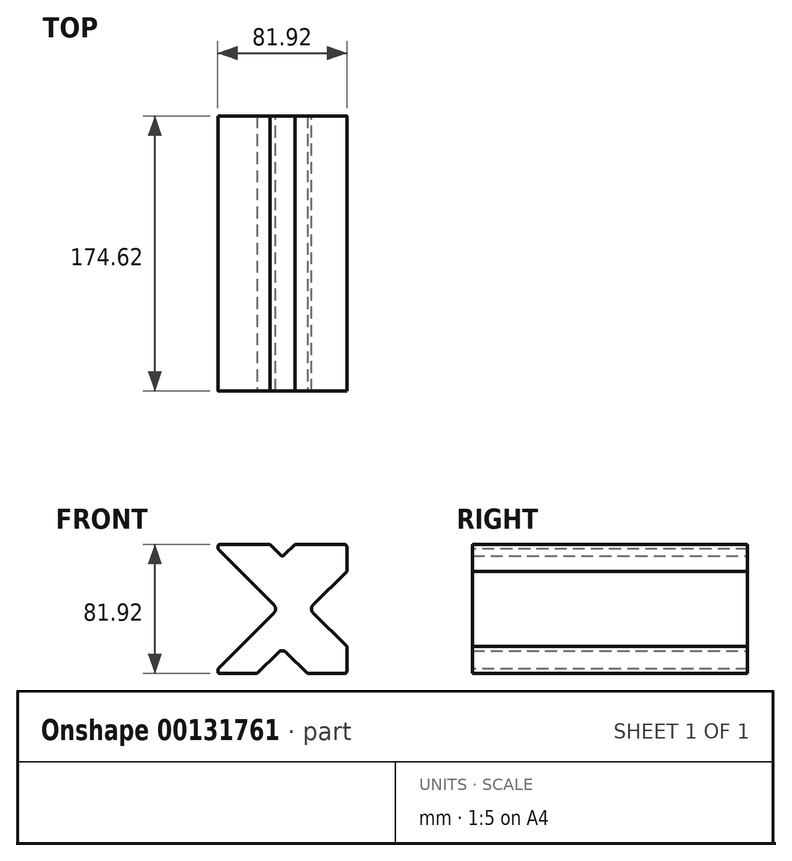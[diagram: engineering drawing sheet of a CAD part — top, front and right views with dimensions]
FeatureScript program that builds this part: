
annotation { "Feature Type Name" : "Feature", "Feature Type Description" : "" }
export const myFeature = defineFeature(function(context is Context, id is Id, definition is map)
    precondition{}
    {
        {
            var Q0;
            Q0=qCreatedBy(makeId("Front.planeOp"),FACE);
            var sketch = newSketch(context, id + "F0", { "sketchPlane" : qUnion([Q0])});
            skLineSegment(sketch, "E0.bottom", {"start": v(40.96, -40.96) * mm, "end": v(-40.96, -40.96) * mm});
            skLineSegment(sketch, "E0.top", {"start": v(40.96, 40.96) * mm, "end": v(-40.96, 40.96) * mm});
            skLineSegment(sketch, "E0.left", {"start": v(40.96, -40.96) * mm, "end": v(40.96, 40.96) * mm});
            skLineSegment(sketch, "E0.right", {"start": v(-40.96, -40.96) * mm, "end": v(-40.96, 40.96) * mm});
            skPoint(sketch, "E0.middle", {"position": v(0, 0) * mm});
            skSolve(sketch);
        }
        {
            var Q0;
            Q0 = qSketchRegion(id + "F0", true);
            extrude(context, id + "F1", {"entities" : qUnion([Q0]), "depth" : 174.62 * mm, "offsetDistance" : 25.4 * mm});
        }
        {
            var Q0;
            Q0=makeQuery(id+"F1.opExtrude","CAP_FACE",FACE,{"disambiguationData":[OSD([sQuery(id+"F0.wireOp",EDGE,"E0.bottom"),sQuery(id+"F0.wireOp",EDGE,"E0.top"),sQuery(id+"F0.wireOp",EDGE,"E0.left"),sQuery(id+"F0.wireOp",EDGE,"E0.right")])],"isStart":false});
            var sketch = newSketch(context, id + "F2", { "sketchPlane" : qUnion([Q0])});
            skLineSegment(sketch, "E1", {"start": v(-7.94, 40.96) * mm, "end": v(0, 33.02) * mm});
            skLineSegment(sketch, "E2", {"start": v(0, 33.02) * mm, "end": v(7.94, 40.96) * mm});
            skLineSegment(sketch, "E3", {"start": v(7.94, 40.96) * mm, "end": v(-7.94, 40.96) * mm});
            skSolve(sketch);
        }
        {
            var Q0;
            Q0 = qSketchRegion(id + "F2", true);
            extrude(context, id + "F3", {"entities" : qUnion([Q0]), "operationType" : NewBodyOperationType.REMOVE, "endBound" : BoundingType.THROUGH_ALL, "oppositeDirection" : true, "depth" : 25.4 * mm, "offsetDistance" : 25.4 * mm});
        }
        {
            var Q0;
            Q0=makeQuery(id+"F1.opExtrude","CAP_FACE",FACE,{"disambiguationData":[OSD([sQuery(id+"F0.wireOp",EDGE,"E0.bottom"),sQuery(id+"F0.wireOp",EDGE,"E0.top"),sQuery(id+"F0.wireOp",EDGE,"E0.left"),sQuery(id+"F0.wireOp",EDGE,"E0.right")])],"isStart":false});
            var sketch = newSketch(context, id + "F4", { "sketchPlane" : qUnion([Q0])});
            skLineSegment(sketch, "E4", {"start": v(-15.87, -40.96) * mm, "end": v(0, -25.08) * mm});
            skLineSegment(sketch, "E5", {"start": v(0, -25.08) * mm, "end": v(15.88, -40.96) * mm});
            skLineSegment(sketch, "E6", {"start": v(15.88, -40.96) * mm, "end": v(-15.87, -40.96) * mm});
            skSolve(sketch);
        }
        {
            var Q0;
            Q0 = qSketchRegion(id + "F4", true);
            extrude(context, id + "F5", {"entities" : qUnion([Q0]), "operationType" : NewBodyOperationType.REMOVE, "endBound" : BoundingType.THROUGH_ALL, "oppositeDirection" : true, "depth" : 25.4 * mm, "offsetDistance" : 25.4 * mm});
        }
        {
            var Q0;
            Q0=makeQuery(id+"F1.opExtrude","CAP_FACE",FACE,{"disambiguationData":[OSD([sQuery(id+"F0.wireOp",EDGE,"E0.bottom"),sQuery(id+"F0.wireOp",EDGE,"E0.top"),sQuery(id+"F0.wireOp",EDGE,"E0.left"),sQuery(id+"F0.wireOp",EDGE,"E0.right")])],"isStart":false});
            var sketch = newSketch(context, id + "F6", { "sketchPlane" : qUnion([Q0])});
            skLineSegment(sketch, "E7", {"start": v(-40.96, 38.1) * mm, "end": v(-2.86, 0) * mm});
            skLineSegment(sketch, "E8", {"start": v(-2.86, 0) * mm, "end": v(-40.96, -38.1) * mm});
            skLineSegment(sketch, "E9", {"start": v(-40.96, -38.1) * mm, "end": v(-40.96, 38.1) * mm});
            skSolve(sketch);
        }
        {
            var Q0;
            Q0 = qSketchRegion(id + "F6", true);
            extrude(context, id + "F7", {"entities" : qUnion([Q0]), "operationType" : NewBodyOperationType.REMOVE, "endBound" : BoundingType.THROUGH_ALL, "oppositeDirection" : true, "depth" : 25.4 * mm, "offsetDistance" : 25.4 * mm});
        }
        {
            var Q0;
            {var subQ2=sQuery(id+"F2.wireOp",EDGE,"E1");Q0=makeQuery(id+"F2.imprint","IMPRINT",FACE,{"disambiguationData":[TD([[makeQuery(id+"F2.imprint","IMPRINT",EDGE,{"derivedFrom":subQ2}),-1.0]])]});}
            var sketch = newSketch(context, id + "F8", { "sketchPlane" : qUnion([Q0])});
            skLineSegment(sketch, "E10", {"start": v(40.96, 23.81) * mm, "end": v(17.14, 0) * mm});
            skLineSegment(sketch, "E11", {"start": v(17.14, 0) * mm, "end": v(40.96, -23.81) * mm});
            skLineSegment(sketch, "E12", {"start": v(40.96, -23.81) * mm, "end": v(40.96, 23.81) * mm});
            skSolve(sketch);
        }
        {
            var Q0;
            Q0 = qSketchRegion(id + "F8", true);
            extrude(context, id + "F9", {"entities" : qUnion([Q0]), "operationType" : NewBodyOperationType.REMOVE, "endBound" : BoundingType.THROUGH_ALL, "oppositeDirection" : true, "depth" : 25.4 * mm, "offsetDistance" : 25.4 * mm});
        }
        {
            var Q0;
            Q0=makeQuery(id+"F3.boolean.opBoolean","COPY",EDGE,{"derivedFrom":makeQuery(id+"F3.opExtrude","SWEPT_EDGE",EDGE,{"disambiguationData":[OSD([sQuery(id+"F0.wireOp",EDGE,"E0.top"),sQuery(id+"F2.wireOp",EDGE,"E1"),sQuery(id+"F2.wireOp",EDGE,"E3")])]})});
            var Q1;
            Q1=makeQuery(id+"F3.boolean.opBoolean","COPY",EDGE,{"derivedFrom":makeQuery(id+"F3.opExtrude","SWEPT_EDGE",EDGE,{"disambiguationData":[OSD([sQuery(id+"F0.wireOp",EDGE,"E0.top"),sQuery(id+"F2.wireOp",EDGE,"E2"),sQuery(id+"F2.wireOp",EDGE,"E3")])]})});
            var Q2;
            Q2=makeQuery(id+"F1.opExtrude","SWEPT_EDGE",EDGE,{"disambiguationData":[OSD([sQuery(id+"F0.wireOp",EDGE,"E0.top"),sQuery(id+"F0.wireOp",EDGE,"E0.left")])]});
            var Q3;
            Q3=makeQuery(id+"F9.boolean.opBoolean","COPY",EDGE,{"derivedFrom":makeQuery(id+"F9.opExtrude","SWEPT_EDGE",EDGE,{"disambiguationData":[OSD([sQuery(id+"F0.wireOp",EDGE,"E0.left"),sQuery(id+"F8.wireOp",EDGE,"E10"),sQuery(id+"F8.wireOp",EDGE,"E12")])]})});
            var Q4;
            Q4=makeQuery(id+"F9.boolean.opBoolean","COPY",EDGE,{"derivedFrom":makeQuery(id+"F9.opExtrude","SWEPT_EDGE",EDGE,{"disambiguationData":[OSD([sQuery(id+"F0.wireOp",EDGE,"E0.left"),sQuery(id+"F8.wireOp",EDGE,"E11"),sQuery(id+"F8.wireOp",EDGE,"E12")])]})});
            var Q5;
            Q5=makeQuery(id+"F1.opExtrude","SWEPT_EDGE",EDGE,{"disambiguationData":[OSD([sQuery(id+"F0.wireOp",EDGE,"E0.bottom"),sQuery(id+"F0.wireOp",EDGE,"E0.left")])]});
            var Q6;
            Q6=makeQuery(id+"F5.boolean.opBoolean","COPY",EDGE,{"derivedFrom":makeQuery(id+"F5.opExtrude","SWEPT_EDGE",EDGE,{"disambiguationData":[OSD([sQuery(id+"F0.wireOp",EDGE,"E0.bottom"),sQuery(id+"F4.wireOp",EDGE,"E5"),sQuery(id+"F4.wireOp",EDGE,"E6")])]})});
            var Q7;
            Q7=makeQuery(id+"F5.boolean.opBoolean","COPY",EDGE,{"derivedFrom":makeQuery(id+"F5.opExtrude","SWEPT_EDGE",EDGE,{"disambiguationData":[OSD([sQuery(id+"F0.wireOp",EDGE,"E0.bottom"),sQuery(id+"F4.wireOp",EDGE,"E4"),sQuery(id+"F4.wireOp",EDGE,"E6")])]})});
            var Q8;
            Q8=makeQuery(id+"F1.opExtrude","SWEPT_EDGE",EDGE,{"disambiguationData":[OSD([sQuery(id+"F0.wireOp",EDGE,"E0.bottom"),sQuery(id+"F0.wireOp",EDGE,"E0.right")])]});
            var Q9;
            Q9=makeQuery(id+"F7.boolean.opBoolean","COPY",EDGE,{"derivedFrom":makeQuery(id+"F7.opExtrude","SWEPT_EDGE",EDGE,{"disambiguationData":[OSD([sQuery(id+"F0.wireOp",EDGE,"E0.right"),sQuery(id+"F6.wireOp",EDGE,"E8"),sQuery(id+"F6.wireOp",EDGE,"E9")])]})});
            var Q10;
            Q10=makeQuery(id+"F7.boolean.opBoolean","COPY",EDGE,{"derivedFrom":makeQuery(id+"F7.opExtrude","SWEPT_EDGE",EDGE,{"disambiguationData":[OSD([sQuery(id+"F0.wireOp",EDGE,"E0.right"),sQuery(id+"F6.wireOp",EDGE,"E7"),sQuery(id+"F6.wireOp",EDGE,"E9")])]})});
            var Q11;
            Q11=makeQuery(id+"F1.opExtrude","SWEPT_EDGE",EDGE,{"disambiguationData":[OSD([sQuery(id+"F0.wireOp",EDGE,"E0.top"),sQuery(id+"F0.wireOp",EDGE,"E0.right")])]});
            fillet(context, id + "F10", {"entities" : qUnion([Q0, Q1, Q2, Q3, Q4, Q5, Q6, Q7, Q8, Q9, Q10, Q11]), "radius" : 1.27 * mm, "tangentPropagation" : true, "allowEdgeOverflow" : false});
        }
        {
            var Q0;
            Q0=makeQuery(id+"F3.boolean.opBoolean","COPY",EDGE,{"derivedFrom":makeQuery(id+"F3.opExtrude","SWEPT_EDGE",EDGE,{"disambiguationData":[OSD([sQuery(id+"F2.wireOp",EDGE,"E1"),sQuery(id+"F2.wireOp",EDGE,"E2")])]})});
            fillet(context, id + "F11", {"entities" : qUnion([Q0]), "radius" : 1.78 * mm, "tangentPropagation" : true, "allowEdgeOverflow" : false});
        }
        {
            var Q0;
            Q0=makeQuery(id+"F5.boolean.opBoolean","COPY",EDGE,{"derivedFrom":makeQuery(id+"F5.opExtrude","SWEPT_EDGE",EDGE,{"disambiguationData":[OSD([sQuery(id+"F4.wireOp",EDGE,"E4"),sQuery(id+"F4.wireOp",EDGE,"E5")])]})});
            var Q1;
            Q1=makeQuery(id+"F9.boolean.opBoolean","COPY",EDGE,{"derivedFrom":makeQuery(id+"F9.opExtrude","SWEPT_EDGE",EDGE,{"disambiguationData":[OSD([sQuery(id+"F8.wireOp",EDGE,"E10"),sQuery(id+"F8.wireOp",EDGE,"E11")])]})});
            var Q2;
            Q2=makeQuery(id+"F7.boolean.opBoolean","COPY",EDGE,{"derivedFrom":makeQuery(id+"F7.opExtrude","SWEPT_EDGE",EDGE,{"disambiguationData":[OSD([sQuery(id+"F6.wireOp",EDGE,"E7"),sQuery(id+"F6.wireOp",EDGE,"E8")])]})});
            fillet(context, id + "F12", {"entities" : qUnion([Q0, Q1, Q2]), "radius" : 3.43 * mm, "tangentPropagation" : true, "allowEdgeOverflow" : false});
        }
    });
